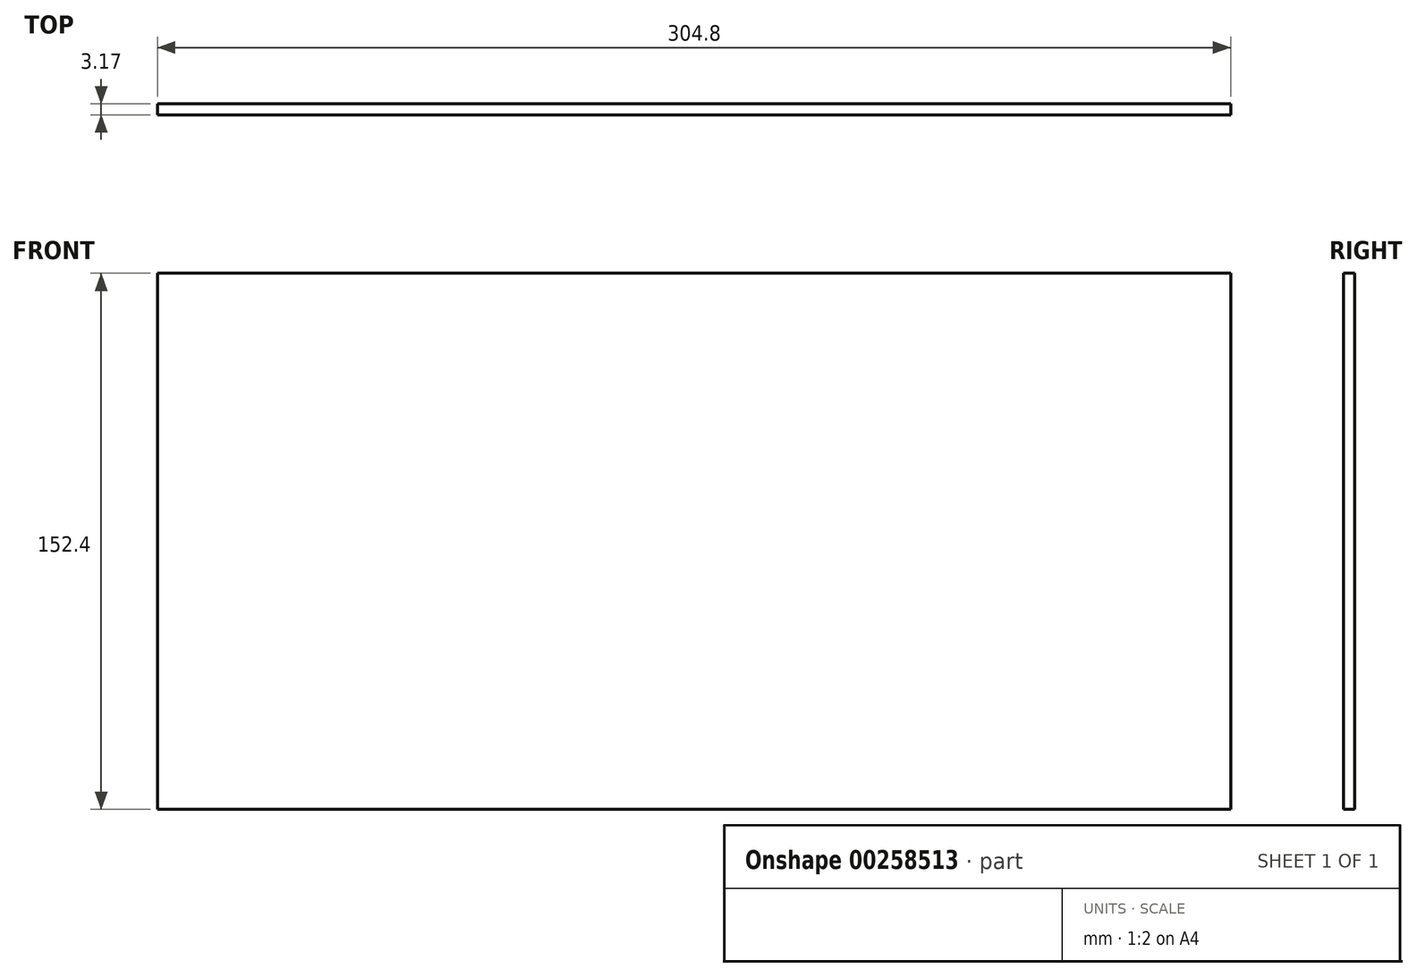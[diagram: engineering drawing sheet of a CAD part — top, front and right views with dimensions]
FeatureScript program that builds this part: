
annotation { "Feature Type Name" : "Feature", "Feature Type Description" : "" }
export const myFeature = defineFeature(function(context is Context, id is Id, definition is map)
    precondition{}
    {
        {
            var Q0;
            Q0=qCreatedBy(makeId("Front.planeOp"),FACE);
            var sketch = newSketch(context, id + "F0", { "sketchPlane" : qUnion([Q0])});
            skLineSegment(sketch, "E0.bottom", {"start": v(152.4, 76.2) * mm, "end": v(-152.4, 76.2) * mm});
            skLineSegment(sketch, "E0.top", {"start": v(152.4, -76.2) * mm, "end": v(-152.4, -76.2) * mm});
            skLineSegment(sketch, "E0.left", {"start": v(152.4, 76.2) * mm, "end": v(152.4, -76.2) * mm});
            skLineSegment(sketch, "E0.right", {"start": v(-152.4, 76.2) * mm, "end": v(-152.4, -76.2) * mm});
            skPoint(sketch, "E0.middle", {"position": v(0, 0) * mm});
            skSolve(sketch);
        }
        {
            var Q0;
            Q0 = qSketchRegion(id + "F0", true);
            extrude(context, id + "F1", {"entities" : qUnion([Q0]), "depth" : 3.17 * mm});
        }
    });
